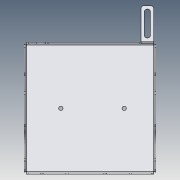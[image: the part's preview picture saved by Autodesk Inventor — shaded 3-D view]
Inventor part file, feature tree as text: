
AUTODESK INVENTOR PART (.ipt)
format: ipt  version: 2020.5 (Build 245400000, 400)  size: 501,760 bytes
history: native  units: mm
features: sketch x11, other x11, sheet_metal_op x7, projected_geometry x6, hole x1, extrude x1, chamfer x1
ambient origin geometry x8: Origin, YZ Plane, XZ Plane, XY Plane, X Axis, Y Axis, Z Axis, Center Point
bodies: Solid1 (feature_tree)
feature tree (38):
  sheet_metal_op  "Face1"
  sheet_metal_op  "Flange1"
  hole  "Hole1"  [1 undecoded]
  extrude  "Extrusion1"  Depth=1.0mm
  sheet_metal_op  "Flange4"
  chamfer  "Corner Round4"
  sketch  "Sketch2"  dims[d0=102.0mm d1=102.0mm]
  other  "Plate1"
  sketch  "Sketch3"  dims[d2=1.0mm d3=1.0mm]
  other  "Plate2"
  sheet_metal_op  "Bend1"
  sheet_metal_op  "Corner1"
  sketch  "Sketch4"  dims[d4=0.5mm]
  projected_geometry  "Projected Loop1"
  sketch  "Sketch6"  dims[d5=2.0mm]
  projected_geometry  "Projected Loop3"
  sketch  "Sketch7"  dims[d6=1.0mm]
  projected_geometry  "Projected Loop4"
  sketch  "Sketch8"  dims[d7=69.4mm d8=90.0deg d9=1.0mm]
  projected_geometry  "Projected Loop5"
  sketch  "Sketch15"  dims[d10=4.0mm]
  sketch  "Sketch19"  dims[d11=1.0mm]
  projected_geometry  "Projected Loop6"
  sketch  "Sketch20"  dims[d12=1.0mm]
  other  "Plate5"
  sheet_metal_op  "Bend4"
  sheet_metal_op  "Corner4"
  sketch  "Sketch21"  dims[d13=18.0mm d14=60.0mm]
  projected_geometry  "Projected Loop7"
  sketch  "Sketch22"  dims[d22=18.0mm d23=60.0mm d24=28.293mm d25=18.0mm d26=60.0mm d27=78.293mm d28=1.0mm d29=0.0mm d38=13.5mm d40=8.373mm d41=1.0mm d42=0.0mm d51=2.0mm d53=2.0mm d55=35.293mm d56=44.043mm d61=94.043mm d62=85.293mm d64=4.0mm d65=4.0mm d66=60.0mm d68=8.0mm d69=4.0mm d70=23.293mm d75=60.0mm d76=12.92mm d78=30.833mm d79=1.0mm d80=0.0mm d82=23.232mm d88=1.0mm d89=0.0mm d91=70.0mm d92=25.0mm d93=12.5mm d95=38.65mm d96=40.306mm d97=43.025mm d98=41.55mm d99=43.025mm d100=41.55mm d101=29.0mm d102=23.251086mm d113=27.0mm d114=3.5mm d115=6.0mm d116=4.0mm d117=2.0mm d118=90.0deg d119=1.0mm d120=20.594885mm d123=1.0mm d124=1.0mm d125=100.0mm d126=100.585786mm d127=50.0mm d128=23.0mm d130=50.0mm d140=29.0mm d148=10.0mm d149=27.560906mm d150=30.0mm d151=1.0mm d152=0.0mm d175=75.463mm d176=1.0mm d177=1.0mm d178=0.0mm d179=1.0mm d180=0.5mm d181=2.0mm d182=1.0mm d183=30.0mm d184=90.0deg d185=1.0mm d186=4.0mm d187=1.0mm d188=1.0mm d189=5.0mm d190=18.0mm d191=1.0mm d192=0.0mm d193=8.373mm d194=35.5mm d195=1.0mm d196=0.0mm d197=2.0mm]
  other  "Cut1"
  other  "Cut2"
  other  "Cut3"
  other  "Cut4"
  other  "Cut8"
  other  "Cut9"
  other  "Cut10"
  other  "Definition1"
note: 1 required parameter value undecoded (feature->parameter linkage not recoverable at this tier; creation-order binding heuristic only, values carry confidence <= 0.55)
